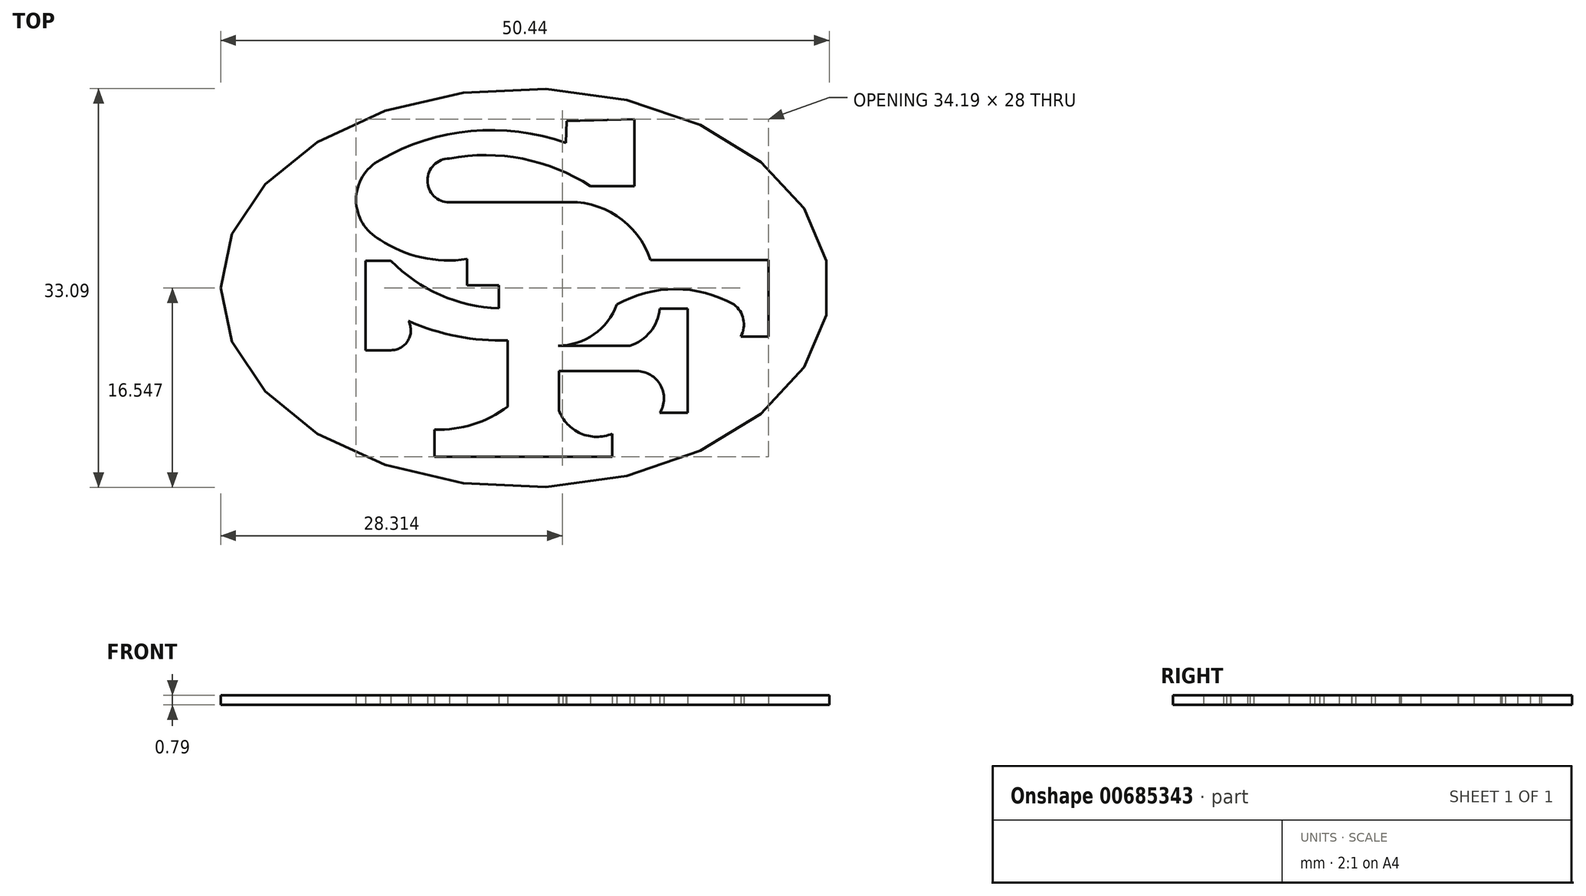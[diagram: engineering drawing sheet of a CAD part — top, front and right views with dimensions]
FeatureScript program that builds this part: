
annotation { "Feature Type Name" : "Feature", "Feature Type Description" : "" }
export const myFeature = defineFeature(function(context is Context, id is Id, definition is map)
    precondition{}
    {
        {
            var Q0;
            Q0=qCreatedBy(makeId("Top.planeOp"),FACE);
            var sketch = newSketch(context, id + "F0", { "sketchPlane" : qUnion([Q0])});
            skArc(sketch, "E0", {"start": v(41.68, -26.21) * mm, "mid": v(33.83, -25.24) * mm, "end": v(26.28, -27.64) * mm});
            skArc(sketch, "E1", {"start": v(26.28, -27.64) * mm, "mid": v(24.3, -30.94) * mm, "end": v(26.28, -34.24) * mm});
            skArc(sketch, "E2", {"start": v(26.28, -34.24) * mm, "mid": v(29.73, -35.72) * mm, "end": v(33.5, -35.85) * mm});
            skArc(sketch, "E3", {"start": v(27.2, -36) * mm, "mid": v(31.28, -38.83) * mm, "end": v(36.12, -39.94) * mm});
            skLineSegment(sketch, "E4", {"start": v(27.2, -36) * mm, "end": v(25.1, -36) * mm});
            skLineSegment(sketch, "E5", {"start": v(25.1, -36) * mm, "end": v(25.1, -43.41) * mm});
            skLineSegment(sketch, "E6", {"start": v(25.1, -43.41) * mm, "end": v(27.2, -43.41) * mm});
            skArc(sketch, "E7", {"start": v(27.2, -43.41) * mm, "mid": v(28.6, -42.62) * mm, "end": v(28.64, -41) * mm});
            skArc(sketch, "E8", {"start": v(28.64, -41) * mm, "mid": v(32.67, -42.25) * mm, "end": v(36.87, -42.6) * mm});
            skLineSegment(sketch, "E9", {"start": v(36.87, -42.6) * mm, "end": v(36.87, -48.09) * mm});
            skArc(sketch, "E10", {"start": v(30.8, -49.99) * mm, "mid": v(34, -49.57) * mm, "end": v(36.87, -48.09) * mm});
            skLineSegment(sketch, "E11", {"start": v(30.8, -49.99) * mm, "end": v(30.8, -52.24) * mm});
            skLineSegment(sketch, "E12", {"start": v(30.8, -52.24) * mm, "end": v(45.53, -52.24) * mm});
            skLineSegment(sketch, "E13", {"start": v(45.53, -52.24) * mm, "end": v(45.53, -50.34) * mm});
            skArc(sketch, "E14", {"start": v(41.12, -48.4) * mm, "mid": v(42.9, -50.31) * mm, "end": v(45.53, -50.34) * mm});
            skLineSegment(sketch, "E15", {"start": v(41.12, -48.4) * mm, "end": v(41.12, -45.15) * mm});
            skLineSegment(sketch, "E16", {"start": v(41.12, -45.15) * mm, "end": v(47.56, -45.15) * mm});
            skArc(sketch, "E17", {"start": v(49.48, -48.6) * mm, "mid": v(49.54, -46.31) * mm, "end": v(47.56, -45.15) * mm});
            skLineSegment(sketch, "E18", {"start": v(51.78, -48.6) * mm, "end": v(51.78, -39.97) * mm});
            skLineSegment(sketch, "E19", {"start": v(51.78, -39.97) * mm, "end": v(49.48, -39.97) * mm});
            skArc(sketch, "E20", {"start": v(46.99, -43.04) * mm, "mid": v(48.7, -41.88) * mm, "end": v(49.48, -39.97) * mm});
            skLineSegment(sketch, "E21", {"start": v(46.99, -43.04) * mm, "end": v(41.04, -43.04) * mm});
            skArc(sketch, "E22", {"start": v(55.61, -39.63) * mm, "mid": v(50.77, -38.34) * mm, "end": v(45.92, -39.63) * mm});
            skArc(sketch, "E23", {"start": v(56.2, -42.27) * mm, "mid": v(56.4, -40.84) * mm, "end": v(55.61, -39.63) * mm});
            skLineSegment(sketch, "E24", {"start": v(56.2, -42.27) * mm, "end": v(58.5, -42.27) * mm});
            skLineSegment(sketch, "E25", {"start": v(58.5, -42.27) * mm, "end": v(58.5, -35.95) * mm});
            skLineSegment(sketch, "E26", {"start": v(58.5, -35.95) * mm, "end": v(48.7, -35.95) * mm});
            skPoint(sketch, "E26.endSnap0", {"position": v(48.7, -41.88) * mm});
            skArc(sketch, "E27", {"start": v(48.7, -35.95) * mm, "mid": v(45.9, -32.27) * mm, "end": v(41.43, -31.15) * mm});
            skLineSegment(sketch, "E28", {"start": v(41.43, -31.15) * mm, "end": v(32.03, -31.15) * mm});
            skArc(sketch, "E29", {"start": v(32.03, -27.51) * mm, "mid": v(30.21, -29.33) * mm, "end": v(32.03, -31.15) * mm});
            skArc(sketch, "E30", {"start": v(43.73, -29.81) * mm, "mid": v(38.1, -27.53) * mm, "end": v(32.03, -27.51) * mm});
            skLineSegment(sketch, "E31", {"start": v(43.73, -29.81) * mm, "end": v(47.37, -29.81) * mm});
            skLineSegment(sketch, "E32", {"start": v(41.68, -26.21) * mm, "end": v(41.74, -24.4) * mm});
            skLineSegment(sketch, "E33", {"start": v(47.37, -29.81) * mm, "end": v(47.37, -24.24) * mm});
            skLineSegment(sketch, "E34", {"start": v(47.37, -24.24) * mm, "end": v(41.74, -24.4) * mm});
            skLineSegment(sketch, "E35", {"start": v(33.5, -35.85) * mm, "end": v(33.5, -38.02) * mm});
            skLineSegment(sketch, "E36", {"start": v(33.5, -38.02) * mm, "end": v(36.12, -38.02) * mm});
            skLineSegment(sketch, "E37", {"start": v(36.12, -38.02) * mm, "end": v(36.12, -39.94) * mm});
            skPoint(sketch, "E38.end.orphan", {"position": v(41.7, -35.85) * mm});
            skPoint(sketch, "E38.start.orphan", {"position": v(41.7, -38.9) * mm});
            skLineSegment(sketch, "E39", {"start": v(49.48, -48.6) * mm, "end": v(51.78, -48.6) * mm});
            skArc(sketch, "E40", {"start": v(41.04, -43.04) * mm, "mid": v(44.02, -42.1) * mm, "end": v(45.92, -39.63) * mm});
            skPoint(sketch, "E41.startSnap0", {"position": v(24.3, -30.94) * mm});
            skPoint(sketch, "E42.endSnap0", {"position": v(38.16, -52.24) * mm});
            skEllipse(sketch, "E43", {"center": v(38.3, -38.24) * mm, "majorRadius": 25.22 * mm, "minorRadius": 16.54 * mm, "majorAxis": v(-1, 0)});
            skSolve(sketch);
        }
        {
            var Q0;
            {var subQ31=sQuery(id+"F0.wireOp",EDGE,"E1");Q0=makeQuery(id+"F0.imprint","IMPRINT",FACE,{"disambiguationData":[TD([[makeQuery(id+"F0.imprint","IMPRINT",EDGE,{"derivedFrom":subQ31}),-1.0]])]});}
            extrude(context, id + "F1", {"entities" : qUnion([Q0]), "depth" : 0.8 * mm, "offsetDistance" : 25.4 * mm});
        }
    });
